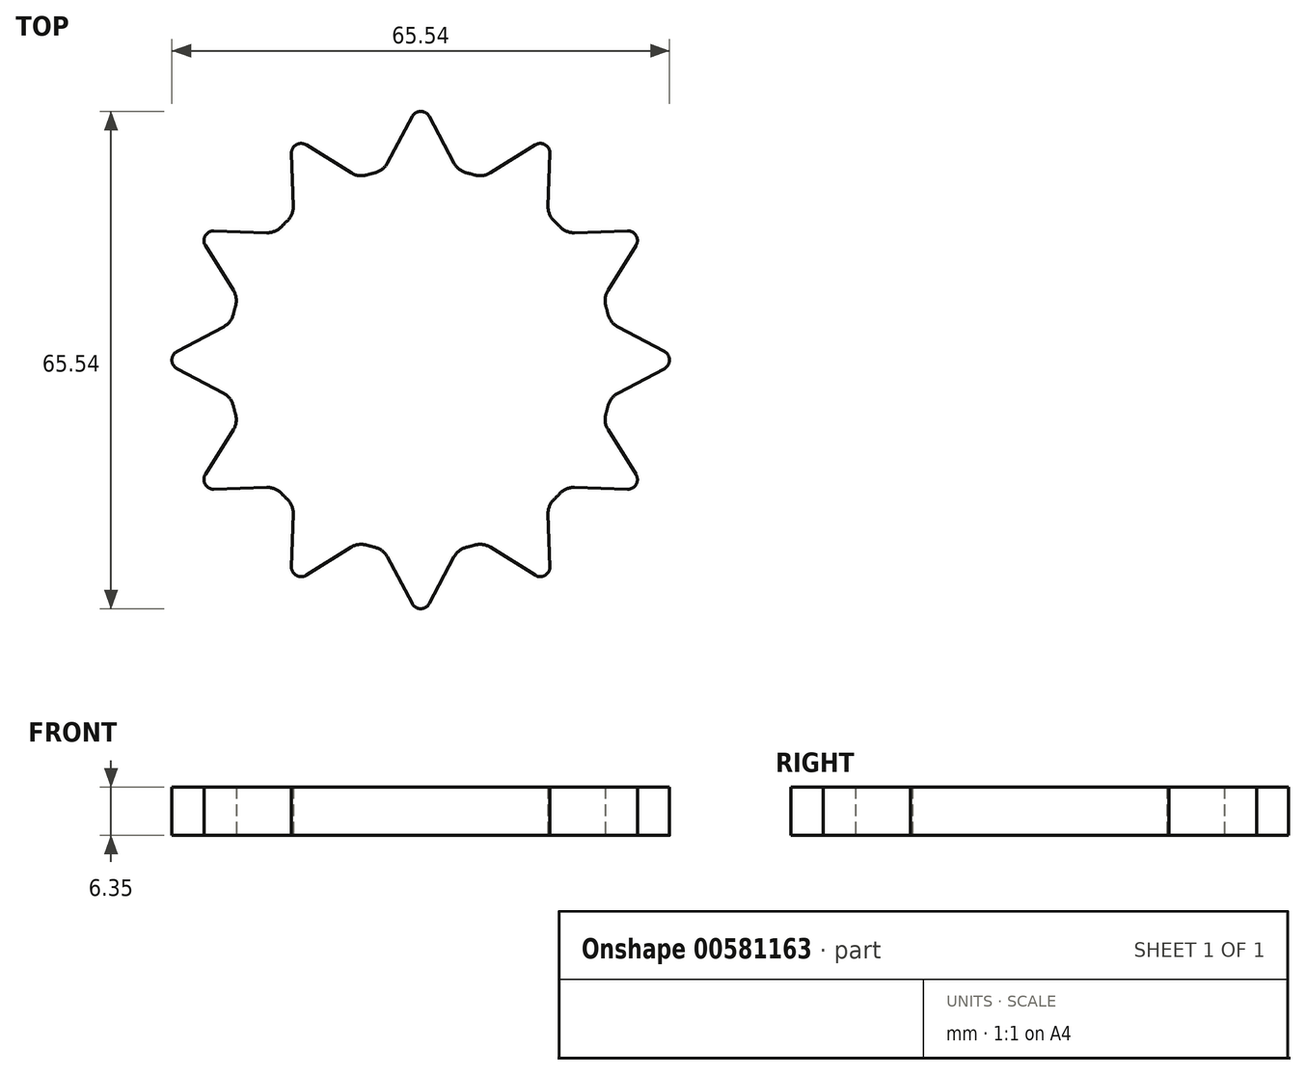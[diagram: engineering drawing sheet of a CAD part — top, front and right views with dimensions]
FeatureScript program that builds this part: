
annotation { "Feature Type Name" : "Feature", "Feature Type Description" : "" }
export const myFeature = defineFeature(function(context is Context, id is Id, definition is map)
    precondition{}
    {
        {
            var Q0;
            Q0=qCreatedBy(makeId("Top.planeOp"),FACE);
            var sketch = newSketch(context, id + "F0", { "sketchPlane" : qUnion([Q0])});
            skArc(sketch, "E0", {"start": v(-6.03, 24.67) * mm, "mid": v(0, -25.4) * mm, "end": v(6.03, 24.67) * mm});
            skLineSegment(sketch, "E1", {"start": v(0, 0) * mm, "end": v(0, 25.4) * mm});
            skLineSegment(sketch, "E2", {"start": v(0, 25.4) * mm, "end": v(0, 31.5) * mm});
            skCircle(sketch, "E3", {"center": v(0, 31.5) * mm, "radius": 1.27 * mm});
            skLineSegment(sketch, "E4", {"start": v(-4.4, 25.95) * mm, "end": v(-1.12, 32.1) * mm});
            skLineSegment(sketch, "E5.MirrorCS", {"start": v(4.4, 25.95) * mm, "end": v(1.12, 32.1) * mm});
            skPoint(sketch, "E6.visualSharp", {"position": v(-4.94, 24.91) * mm});
            skArc(sketch, "E6.filletArc", {"start": v(-6.03, 24.67) * mm, "mid": v(-5.08, 25.14) * mm, "end": v(-4.4, 25.95) * mm});
            skPoint(sketch, "E7.visualSharp", {"position": v(4.94, 24.91) * mm});
            skArc(sketch, "E7.filletArc", {"start": v(4.4, 25.95) * mm, "mid": v(5.08, 25.14) * mm, "end": v(6.03, 24.67) * mm});
            skLineSegment(sketch, "E8.1.0", {"start": v(-16.78, 20.27) * mm, "end": v(-17.02, 27.23) * mm});
            skCircle(sketch, "E8.1.1", {"center": v(-15.75, 27.28) * mm, "radius": 1.27 * mm});
            skLineSegment(sketch, "E8.1.2", {"start": v(-9.17, 24.67) * mm, "end": v(-15.08, 28.35) * mm});
            skArc(sketch, "E8.1.3", {"start": v(-17.56, 18.35) * mm, "mid": v(-16.96, 19.23) * mm, "end": v(-16.78, 20.27) * mm});
            skArc(sketch, "E8.1.4", {"start": v(-9.17, 24.67) * mm, "mid": v(-8.17, 24.3) * mm, "end": v(-7.11, 24.38) * mm});
            skLineSegment(sketch, "E8.2.0", {"start": v(-24.67, 9.17) * mm, "end": v(-28.35, 15.08) * mm});
            skCircle(sketch, "E8.2.1", {"center": v(-27.28, 15.75) * mm, "radius": 1.27 * mm});
            skLineSegment(sketch, "E8.2.2", {"start": v(-20.27, 16.78) * mm, "end": v(-27.23, 17.02) * mm});
            skArc(sketch, "E8.2.3", {"start": v(-24.38, 7.11) * mm, "mid": v(-24.3, 8.17) * mm, "end": v(-24.67, 9.17) * mm});
            skArc(sketch, "E8.2.4", {"start": v(-20.27, 16.78) * mm, "mid": v(-19.23, 16.96) * mm, "end": v(-18.35, 17.56) * mm});
            skLineSegment(sketch, "E8.3.0", {"start": v(-25.95, -4.4) * mm, "end": v(-32.1, -1.12) * mm});
            skCircle(sketch, "E8.3.1", {"center": v(-31.5, 0) * mm, "radius": 1.27 * mm});
            skLineSegment(sketch, "E8.3.2", {"start": v(-25.95, 4.4) * mm, "end": v(-32.1, 1.12) * mm});
            skArc(sketch, "E8.3.3", {"start": v(-24.67, -6.03) * mm, "mid": v(-25.14, -5.08) * mm, "end": v(-25.95, -4.4) * mm});
            skArc(sketch, "E8.3.4", {"start": v(-25.95, 4.4) * mm, "mid": v(-25.14, 5.08) * mm, "end": v(-24.67, 6.03) * mm});
            skLineSegment(sketch, "E8.4.0", {"start": v(-20.27, -16.78) * mm, "end": v(-27.23, -17.02) * mm});
            skCircle(sketch, "E8.4.1", {"center": v(-27.28, -15.75) * mm, "radius": 1.27 * mm});
            skLineSegment(sketch, "E8.4.2", {"start": v(-24.67, -9.17) * mm, "end": v(-28.35, -15.08) * mm});
            skArc(sketch, "E8.4.3", {"start": v(-18.35, -17.56) * mm, "mid": v(-19.23, -16.96) * mm, "end": v(-20.27, -16.78) * mm});
            skArc(sketch, "E8.4.4", {"start": v(-24.67, -9.17) * mm, "mid": v(-24.3, -8.17) * mm, "end": v(-24.38, -7.11) * mm});
            skLineSegment(sketch, "E8.5.0", {"start": v(-9.17, -24.67) * mm, "end": v(-15.08, -28.35) * mm});
            skCircle(sketch, "E8.5.1", {"center": v(-15.75, -27.28) * mm, "radius": 1.27 * mm});
            skLineSegment(sketch, "E8.5.2", {"start": v(-16.78, -20.27) * mm, "end": v(-17.02, -27.23) * mm});
            skArc(sketch, "E8.5.3", {"start": v(-7.11, -24.38) * mm, "mid": v(-8.17, -24.3) * mm, "end": v(-9.17, -24.67) * mm});
            skArc(sketch, "E8.5.4", {"start": v(-16.78, -20.27) * mm, "mid": v(-16.96, -19.23) * mm, "end": v(-17.56, -18.35) * mm});
            skLineSegment(sketch, "E8.6.0", {"start": v(4.4, -25.95) * mm, "end": v(1.12, -32.1) * mm});
            skCircle(sketch, "E8.6.1", {"center": v(0, -31.5) * mm, "radius": 1.27 * mm});
            skLineSegment(sketch, "E8.6.2", {"start": v(-4.4, -25.95) * mm, "end": v(-1.12, -32.1) * mm});
            skArc(sketch, "E8.6.3", {"start": v(6.03, -24.67) * mm, "mid": v(5.08, -25.14) * mm, "end": v(4.4, -25.95) * mm});
            skArc(sketch, "E8.6.4", {"start": v(-4.4, -25.95) * mm, "mid": v(-5.08, -25.14) * mm, "end": v(-6.03, -24.67) * mm});
            skLineSegment(sketch, "E8.7.0", {"start": v(16.78, -20.27) * mm, "end": v(17.02, -27.23) * mm});
            skCircle(sketch, "E8.7.1", {"center": v(15.75, -27.28) * mm, "radius": 1.27 * mm});
            skLineSegment(sketch, "E8.7.2", {"start": v(9.17, -24.67) * mm, "end": v(15.08, -28.35) * mm});
            skArc(sketch, "E8.7.3", {"start": v(17.56, -18.35) * mm, "mid": v(16.96, -19.23) * mm, "end": v(16.78, -20.27) * mm});
            skArc(sketch, "E8.7.4", {"start": v(9.17, -24.67) * mm, "mid": v(8.17, -24.3) * mm, "end": v(7.11, -24.38) * mm});
            skLineSegment(sketch, "E8.8.0", {"start": v(24.67, -9.17) * mm, "end": v(28.35, -15.08) * mm});
            skCircle(sketch, "E8.8.1", {"center": v(27.28, -15.75) * mm, "radius": 1.27 * mm});
            skLineSegment(sketch, "E8.8.2", {"start": v(20.27, -16.78) * mm, "end": v(27.23, -17.02) * mm});
            skArc(sketch, "E8.8.3", {"start": v(24.38, -7.11) * mm, "mid": v(24.3, -8.17) * mm, "end": v(24.67, -9.17) * mm});
            skArc(sketch, "E8.8.4", {"start": v(20.27, -16.78) * mm, "mid": v(19.23, -16.96) * mm, "end": v(18.35, -17.56) * mm});
            skLineSegment(sketch, "E8.9.0", {"start": v(25.95, 4.4) * mm, "end": v(32.1, 1.12) * mm});
            skCircle(sketch, "E8.9.1", {"center": v(31.5, 0) * mm, "radius": 1.27 * mm});
            skLineSegment(sketch, "E8.9.2", {"start": v(25.95, -4.4) * mm, "end": v(32.1, -1.12) * mm});
            skArc(sketch, "E8.9.3", {"start": v(24.67, 6.03) * mm, "mid": v(25.14, 5.08) * mm, "end": v(25.95, 4.4) * mm});
            skArc(sketch, "E8.9.4", {"start": v(25.95, -4.4) * mm, "mid": v(25.14, -5.08) * mm, "end": v(24.67, -6.03) * mm});
            skLineSegment(sketch, "E8.10.0", {"start": v(20.27, 16.78) * mm, "end": v(27.23, 17.02) * mm});
            skCircle(sketch, "E8.10.1", {"center": v(27.28, 15.75) * mm, "radius": 1.27 * mm});
            skLineSegment(sketch, "E8.10.2", {"start": v(24.67, 9.17) * mm, "end": v(28.35, 15.08) * mm});
            skArc(sketch, "E8.10.3", {"start": v(18.35, 17.56) * mm, "mid": v(19.23, 16.96) * mm, "end": v(20.27, 16.78) * mm});
            skArc(sketch, "E8.10.4", {"start": v(24.67, 9.17) * mm, "mid": v(24.3, 8.17) * mm, "end": v(24.38, 7.11) * mm});
            skLineSegment(sketch, "E8.11.0", {"start": v(9.17, 24.67) * mm, "end": v(15.08, 28.35) * mm});
            skCircle(sketch, "E8.11.1", {"center": v(15.75, 27.28) * mm, "radius": 1.27 * mm});
            skLineSegment(sketch, "E8.11.2", {"start": v(16.78, 20.27) * mm, "end": v(17.02, 27.23) * mm});
            skArc(sketch, "E8.11.3", {"start": v(7.11, 24.38) * mm, "mid": v(8.17, 24.3) * mm, "end": v(9.17, 24.67) * mm});
            skArc(sketch, "E8.11.4", {"start": v(16.78, 20.27) * mm, "mid": v(16.96, 19.23) * mm, "end": v(17.56, 18.35) * mm});
            skSolve(sketch);
        }
        {
            var Q0;
            {var subQ25=sQuery(id+"F0.wireOp",EDGE,"E4");Q0=makeQuery(id+"F0.imprint","IMPRINT",FACE,{"disambiguationData":[TD([[makeQuery(id+"F0.imprint","IMPRINT",EDGE,{"derivedFrom":subQ25}),-1.0]])]});}
            var Q1;
            {var subQ2=sQuery(id+"F0.wireOp",EDGE,"E8.1.0");Q1=makeQuery(id+"F0.imprint","IMPRINT",FACE,{"disambiguationData":[TD([[makeQuery(id+"F0.imprint","IMPRINT",EDGE,{"derivedFrom":subQ2}),-1.0]])]});}
            var Q2;
            {var subQ0=sQuery(id+"F0.wireOp",EDGE,"E8.1.1");var subQ1=makeQuery(id+"F0.imprint","INTERSECT",VERTEX,{"derivedFrom":[sQuery(id+"F0.wireOp",EDGE,"E8.1.0"),subQ0]});Q2=makeQuery(id+"F0.imprint","IMPRINT",FACE,{"disambiguationData":[TD([[makeQuery(id+"F0.imprint","IMPRINT",EDGE,{"disambiguationData":[TD([[subQ1,1.0]])],"derivedFrom":subQ0}),1.0]])]});}
            var Q3;
            {var subQ0=sQuery(id+"F0.wireOp",EDGE,"E3");var subQ3=makeQuery(id+"F0.imprint","IMPRINT",VERTEX,{"derivedFrom":subQ0});Q3=makeQuery(id+"F0.imprint","IMPRINT",FACE,{"disambiguationData":[TD([[makeQuery(id+"F0.imprint","IMPRINT",EDGE,{"disambiguationData":[TD([[subQ3,1.0]])],"derivedFrom":subQ0}),1.0]])]});}
            var Q4;
            {var subQ2=sQuery(id+"F0.wireOp",EDGE,"E8.11.0");Q4=makeQuery(id+"F0.imprint","IMPRINT",FACE,{"disambiguationData":[TD([[makeQuery(id+"F0.imprint","IMPRINT",EDGE,{"derivedFrom":subQ2}),-1.0]])]});}
            var Q5;
            {var subQ0=sQuery(id+"F0.wireOp",EDGE,"E8.11.1");var subQ1=makeQuery(id+"F0.imprint","INTERSECT",VERTEX,{"derivedFrom":[sQuery(id+"F0.wireOp",EDGE,"E8.11.0"),subQ0]});Q5=makeQuery(id+"F0.imprint","IMPRINT",FACE,{"disambiguationData":[TD([[makeQuery(id+"F0.imprint","IMPRINT",EDGE,{"disambiguationData":[TD([[subQ1,1.0]])],"derivedFrom":subQ0}),1.0]])]});}
            var Q6;
            {var subQ2=sQuery(id+"F0.wireOp",EDGE,"E8.10.0");Q6=makeQuery(id+"F0.imprint","IMPRINT",FACE,{"disambiguationData":[TD([[makeQuery(id+"F0.imprint","IMPRINT",EDGE,{"derivedFrom":subQ2}),-1.0]])]});}
            var Q7;
            {var subQ2=sQuery(id+"F0.wireOp",EDGE,"E8.9.0");Q7=makeQuery(id+"F0.imprint","IMPRINT",FACE,{"disambiguationData":[TD([[makeQuery(id+"F0.imprint","IMPRINT",EDGE,{"derivedFrom":subQ2}),-1.0]])]});}
            var Q8;
            {var subQ0=sQuery(id+"F0.wireOp",EDGE,"E8.9.1");var subQ1=makeQuery(id+"F0.imprint","INTERSECT",VERTEX,{"derivedFrom":[sQuery(id+"F0.wireOp",EDGE,"E8.9.0"),subQ0]});Q8=makeQuery(id+"F0.imprint","IMPRINT",FACE,{"disambiguationData":[TD([[makeQuery(id+"F0.imprint","IMPRINT",EDGE,{"disambiguationData":[TD([[subQ1,1.0]])],"derivedFrom":subQ0}),1.0]])]});}
            var Q9;
            {var subQ0=sQuery(id+"F0.wireOp",EDGE,"E8.10.1");var subQ1=makeQuery(id+"F0.imprint","INTERSECT",VERTEX,{"derivedFrom":[sQuery(id+"F0.wireOp",EDGE,"E8.10.0"),subQ0]});Q9=makeQuery(id+"F0.imprint","IMPRINT",FACE,{"disambiguationData":[TD([[makeQuery(id+"F0.imprint","IMPRINT",EDGE,{"disambiguationData":[TD([[subQ1,1.0]])],"derivedFrom":subQ0}),1.0]])]});}
            var Q10;
            {var subQ1=sQuery(id+"F0.wireOp",EDGE,"E8.8.0");Q10=makeQuery(id+"F0.imprint","IMPRINT",FACE,{"disambiguationData":[TD([[makeQuery(id+"F0.imprint","IMPRINT",EDGE,{"derivedFrom":subQ1}),-1.0]])]});}
            var Q11;
            {var subQ1=sQuery(id+"F0.wireOp",EDGE,"E8.7.0");Q11=makeQuery(id+"F0.imprint","IMPRINT",FACE,{"disambiguationData":[TD([[makeQuery(id+"F0.imprint","IMPRINT",EDGE,{"derivedFrom":subQ1}),-1.0]])]});}
            var Q12;
            {var subQ2=sQuery(id+"F0.wireOp",EDGE,"E8.6.0");Q12=makeQuery(id+"F0.imprint","IMPRINT",FACE,{"disambiguationData":[TD([[makeQuery(id+"F0.imprint","IMPRINT",EDGE,{"derivedFrom":subQ2}),-1.0]])]});}
            var Q13;
            {var subQ2=sQuery(id+"F0.wireOp",EDGE,"E8.5.0");Q13=makeQuery(id+"F0.imprint","IMPRINT",FACE,{"disambiguationData":[TD([[makeQuery(id+"F0.imprint","IMPRINT",EDGE,{"derivedFrom":subQ2}),-1.0]])]});}
            var Q14;
            {var subQ5=sQuery(id+"F0.wireOp",EDGE,"E8.4.0");Q14=makeQuery(id+"F0.imprint","IMPRINT",FACE,{"disambiguationData":[TD([[makeQuery(id+"F0.imprint","IMPRINT",EDGE,{"derivedFrom":subQ5}),-1.0]])]});}
            var Q15;
            {var subQ1=sQuery(id+"F0.wireOp",EDGE,"E8.3.0");Q15=makeQuery(id+"F0.imprint","IMPRINT",FACE,{"disambiguationData":[TD([[makeQuery(id+"F0.imprint","IMPRINT",EDGE,{"derivedFrom":subQ1}),-1.0]])]});}
            var Q16;
            {var subQ1=sQuery(id+"F0.wireOp",EDGE,"E8.2.0");Q16=makeQuery(id+"F0.imprint","IMPRINT",FACE,{"disambiguationData":[TD([[makeQuery(id+"F0.imprint","IMPRINT",EDGE,{"derivedFrom":subQ1}),-1.0]])]});}
            var Q17;
            {var subQ0=sQuery(id+"F0.wireOp",EDGE,"E8.2.1");var subQ1=makeQuery(id+"F0.imprint","INTERSECT",VERTEX,{"derivedFrom":[sQuery(id+"F0.wireOp",EDGE,"E8.2.0"),subQ0]});Q17=makeQuery(id+"F0.imprint","IMPRINT",FACE,{"disambiguationData":[TD([[makeQuery(id+"F0.imprint","IMPRINT",EDGE,{"disambiguationData":[TD([[subQ1,1.0]])],"derivedFrom":subQ0}),1.0]])]});}
            var Q18;
            {var subQ0=sQuery(id+"F0.wireOp",EDGE,"E8.3.1");var subQ1=makeQuery(id+"F0.imprint","INTERSECT",VERTEX,{"derivedFrom":[sQuery(id+"F0.wireOp",EDGE,"E8.3.0"),subQ0]});Q18=makeQuery(id+"F0.imprint","IMPRINT",FACE,{"disambiguationData":[TD([[makeQuery(id+"F0.imprint","IMPRINT",EDGE,{"disambiguationData":[TD([[subQ1,1.0]])],"derivedFrom":subQ0}),1.0]])]});}
            var Q19;
            {var subQ0=sQuery(id+"F0.wireOp",EDGE,"E8.4.1");var subQ1=makeQuery(id+"F0.imprint","INTERSECT",VERTEX,{"derivedFrom":[sQuery(id+"F0.wireOp",EDGE,"E8.4.0"),subQ0]});Q19=makeQuery(id+"F0.imprint","IMPRINT",FACE,{"disambiguationData":[TD([[makeQuery(id+"F0.imprint","IMPRINT",EDGE,{"disambiguationData":[TD([[subQ1,1.0]])],"derivedFrom":subQ0}),1.0]])]});}
            var Q20;
            {var subQ0=sQuery(id+"F0.wireOp",EDGE,"E8.5.1");var subQ1=makeQuery(id+"F0.imprint","INTERSECT",VERTEX,{"derivedFrom":[sQuery(id+"F0.wireOp",EDGE,"E8.5.0"),subQ0]});Q20=makeQuery(id+"F0.imprint","IMPRINT",FACE,{"disambiguationData":[TD([[makeQuery(id+"F0.imprint","IMPRINT",EDGE,{"disambiguationData":[TD([[subQ1,1.0]])],"derivedFrom":subQ0}),1.0]])]});}
            var Q21;
            {var subQ0=sQuery(id+"F0.wireOp",EDGE,"E8.6.1");var subQ1=makeQuery(id+"F0.imprint","INTERSECT",VERTEX,{"derivedFrom":[sQuery(id+"F0.wireOp",EDGE,"E8.6.0"),subQ0]});Q21=makeQuery(id+"F0.imprint","IMPRINT",FACE,{"disambiguationData":[TD([[makeQuery(id+"F0.imprint","IMPRINT",EDGE,{"disambiguationData":[TD([[subQ1,1.0]])],"derivedFrom":subQ0}),1.0]])]});}
            var Q22;
            {var subQ0=sQuery(id+"F0.wireOp",EDGE,"E8.7.1");var subQ1=makeQuery(id+"F0.imprint","INTERSECT",VERTEX,{"derivedFrom":[sQuery(id+"F0.wireOp",EDGE,"E8.7.0"),subQ0]});Q22=makeQuery(id+"F0.imprint","IMPRINT",FACE,{"disambiguationData":[TD([[makeQuery(id+"F0.imprint","IMPRINT",EDGE,{"disambiguationData":[TD([[subQ1,1.0]])],"derivedFrom":subQ0}),1.0]])]});}
            var Q23;
            {var subQ0=sQuery(id+"F0.wireOp",EDGE,"E8.8.1");var subQ1=makeQuery(id+"F0.imprint","INTERSECT",VERTEX,{"derivedFrom":[sQuery(id+"F0.wireOp",EDGE,"E8.8.0"),subQ0]});Q23=makeQuery(id+"F0.imprint","IMPRINT",FACE,{"disambiguationData":[TD([[makeQuery(id+"F0.imprint","IMPRINT",EDGE,{"disambiguationData":[TD([[subQ1,1.0]])],"derivedFrom":subQ0}),1.0]])]});}
            extrude(context, id + "F1", {"entities" : qUnion([Q0, Q1, Q2, Q3, Q4, Q5, Q6, Q7, Q8, Q9, Q10, Q11, Q12, Q13, Q14, Q15, Q16, Q17, Q18, Q19, Q20, Q21, Q22, Q23]), "depth" : 6.35 * mm, "offsetDistance" : 25.4 * mm});
        }
    });
